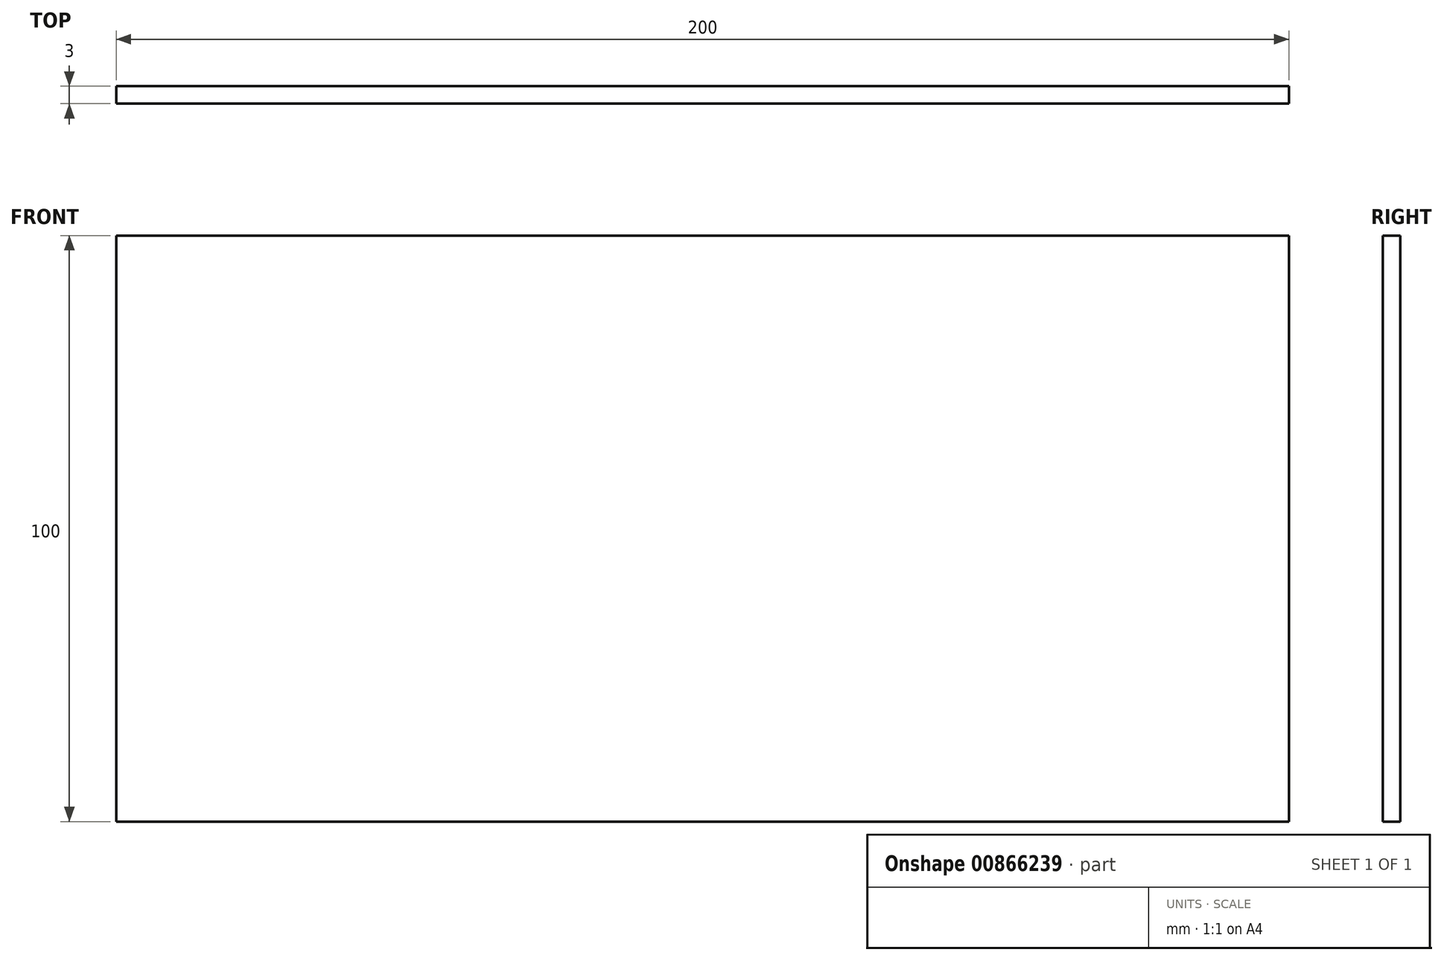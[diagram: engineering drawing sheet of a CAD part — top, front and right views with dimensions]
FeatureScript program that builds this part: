
annotation { "Feature Type Name" : "Feature", "Feature Type Description" : "" }
export const myFeature = defineFeature(function(context is Context, id is Id, definition is map)
    precondition{}
    {
        {
            var Q0;
            Q0=qCreatedBy(makeId("Front.planeOp"),FACE);
            var sketch = newSketch(context, id + "F0", { "sketchPlane" : qUnion([Q0])});
            skLineSegment(sketch, "E0.bottom", {"start": v(-183.98, 13.3) * mm, "end": v(16.02, 13.3) * mm});
            skLineSegment(sketch, "E0.top", {"start": v(-183.98, -86.7) * mm, "end": v(16.02, -86.7) * mm});
            skLineSegment(sketch, "E0.left", {"start": v(-183.98, 13.3) * mm, "end": v(-183.98, -86.7) * mm});
            skLineSegment(sketch, "E0.right", {"start": v(16.02, 13.3) * mm, "end": v(16.02, -86.7) * mm});
            skSolve(sketch);
        }
        {
            var Q0;
            Q0=makeQuery(id+"F0.imprint","IMPRINT",FACE,{"disambiguationData":[TD([[makeQuery(id+"F0.imprint","IMPRINT",EDGE,{"derivedFrom":sQuery(id+"F0.wireOp",EDGE,"E0.bottom")}),-1.0]])]});
            extrude(context, id + "F1", {"entities" : qUnion([Q0]), "depth" : 3 * mm, "offsetDistance" : 25 * mm});
        }
    });
